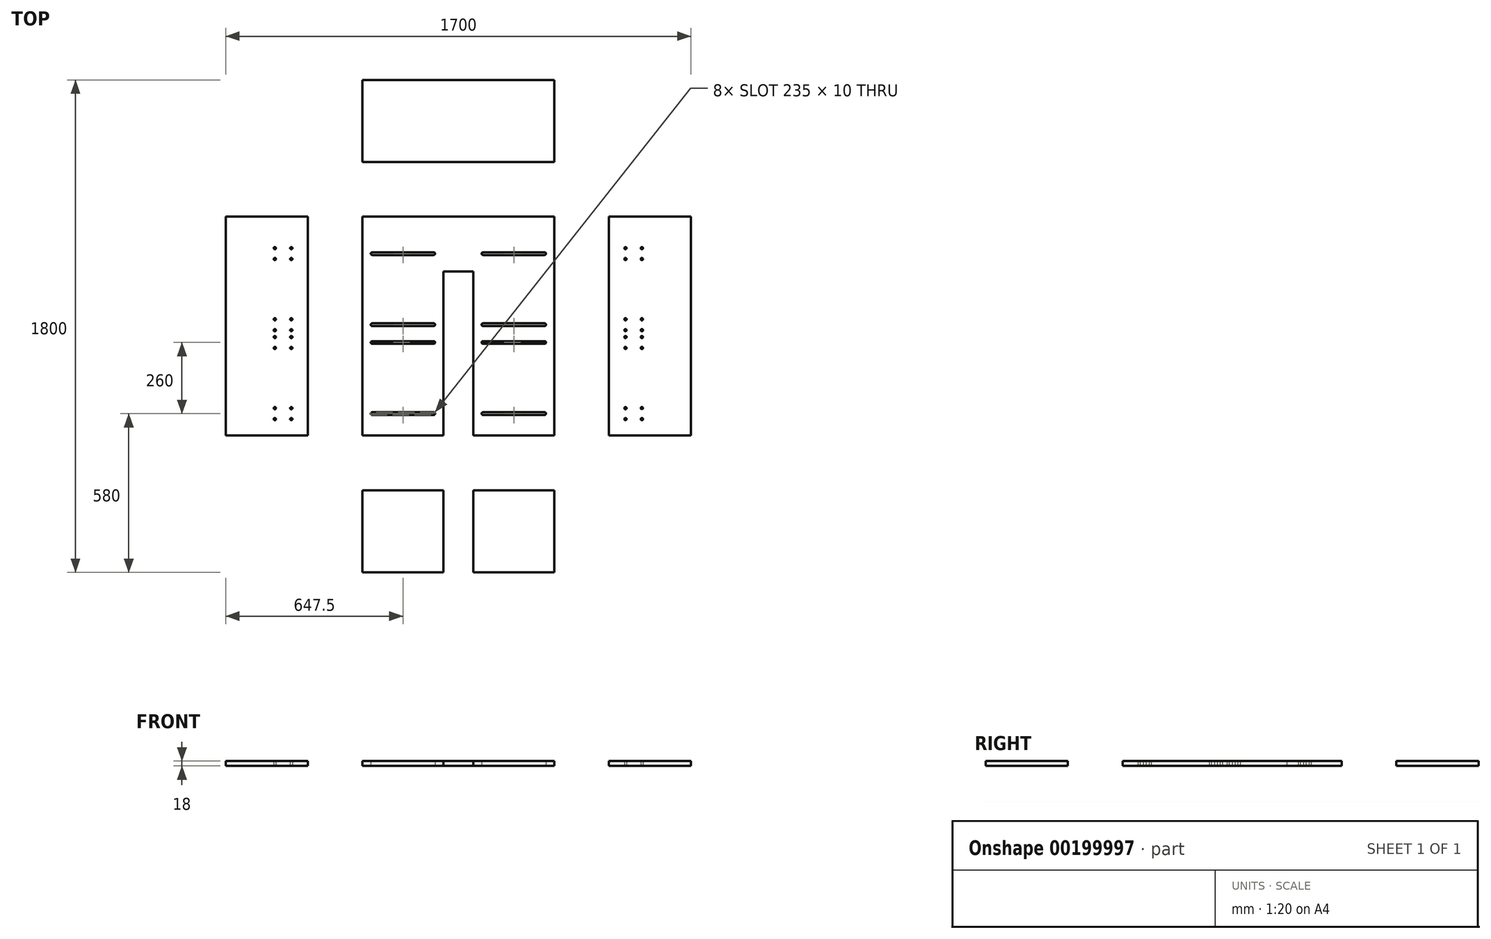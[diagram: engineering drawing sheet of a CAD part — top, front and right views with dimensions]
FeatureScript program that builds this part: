
annotation { "Feature Type Name" : "Feature", "Feature Type Description" : "" }
export const myFeature = defineFeature(function(context is Context, id is Id, definition is map)
    precondition{}
    {
        {
            var Q0;
            Q0=qCreatedBy(makeId("Top.planeOp"),FACE);
            var sketch = newSketch(context, id + "F0", { "sketchPlane" : qUnion([Q0])});
            skLineSegment(sketch, "E0.bottom", {"start": v(0, 0) * mm, "end": v(4000, 0) * mm, "construction": true});
            skLineSegment(sketch, "E0.top", {"start": v(0, 4000) * mm, "end": v(4000, 4000) * mm, "construction": true});
            skLineSegment(sketch, "E0.left", {"start": v(0, 0) * mm, "end": v(0, 4000) * mm, "construction": true});
            skLineSegment(sketch, "E0.right", {"start": v(4000, 0) * mm, "end": v(4000, 4000) * mm, "construction": true});
            skLineSegment(sketch, "E1.bottom", {"start": v(0, 0) * mm, "end": v(1000, 0) * mm, "construction": true});
            skLineSegment(sketch, "E1.top", {"start": v(0, 1000) * mm, "end": v(1000, 1000) * mm, "construction": true});
            skLineSegment(sketch, "E1.left", {"start": v(0, 0) * mm, "end": v(0, 1000) * mm, "construction": true});
            skLineSegment(sketch, "E1.right", {"start": v(1000, 0) * mm, "end": v(1000, 1000) * mm, "construction": true});
            skSolve(sketch);
        }
        {
            var Q0;
            Q0=qCreatedBy(makeId("Top.planeOp"),FACE);
            var sketch = newSketch(context, id + "F1", { "sketchPlane" : qUnion([Q0])});
            skPoint(sketch, "E2", {"position": v(1000, 1000) * mm});
            skLineSegment(sketch, "E3.bottom", {"start": v(1000, 1000) * mm, "end": v(1295, 1000) * mm});
            skLineSegment(sketch, "E3.top", {"start": v(1000, 1800) * mm, "end": v(1700, 1800) * mm});
            skLineSegment(sketch, "E3.left", {"start": v(1000, 1000) * mm, "end": v(1000, 1800) * mm});
            skLineSegment(sketch, "E3.right", {"start": v(1700, 1000) * mm, "end": v(1700, 1800) * mm});
            skLineSegment(sketch, "E4", {"start": v(1405, 1600) * mm, "end": v(1405, 1000) * mm});
            skLineSegment(sketch, "E5", {"start": v(1295, 1000) * mm, "end": v(1295, 1600) * mm});
            skPoint(sketch, "E6", {"position": v(1350, 1000) * mm});
            skLineSegment(sketch, "E7", {"start": v(1295, 1600) * mm, "end": v(1405, 1600) * mm});
            skPoint(sketch, "E8", {"position": v(1350, 1800) * mm});
            skPoint(sketch, "E9", {"position": v(1350, 1600) * mm});
            skLineSegment(sketch, "E10.trimOffspring", {"start": v(1405, 1000) * mm, "end": v(1700, 1000) * mm});
            skLineSegment(sketch, "E11.bottom", {"start": v(800, 1800) * mm, "end": v(500, 1800) * mm});
            skLineSegment(sketch, "E11.top", {"start": v(800, 1000) * mm, "end": v(500, 1000) * mm});
            skLineSegment(sketch, "E11.left", {"start": v(800, 1800) * mm, "end": v(800, 1000) * mm});
            skLineSegment(sketch, "E11.right", {"start": v(500, 1800) * mm, "end": v(500, 1000) * mm});
            skLineSegment(sketch, "E12.bottom", {"start": v(1000, 800) * mm, "end": v(1295, 800) * mm});
            skLineSegment(sketch, "E12.top", {"start": v(1000, 500) * mm, "end": v(1295, 500) * mm});
            skLineSegment(sketch, "E12.left", {"start": v(1000, 800) * mm, "end": v(1000, 500) * mm});
            skLineSegment(sketch, "E12.right", {"start": v(1295, 800) * mm, "end": v(1295, 500) * mm});
            skLineSegment(sketch, "E13.bottom", {"start": v(1000, 2000) * mm, "end": v(1700, 2000) * mm});
            skLineSegment(sketch, "E13.top", {"start": v(1000, 2300) * mm, "end": v(1700, 2300) * mm});
            skLineSegment(sketch, "E13.left", {"start": v(1000, 2000) * mm, "end": v(1000, 2300) * mm});
            skLineSegment(sketch, "E13.right", {"start": v(1700, 2000) * mm, "end": v(1700, 2300) * mm});
            skLineSegment(sketch, "E14.bottom", {"start": v(1405, 800) * mm, "end": v(1700, 800) * mm});
            skLineSegment(sketch, "E14.top", {"start": v(1405, 500) * mm, "end": v(1700, 500) * mm});
            skLineSegment(sketch, "E14.left", {"start": v(1405, 800) * mm, "end": v(1405, 500) * mm});
            skLineSegment(sketch, "E14.right", {"start": v(1700, 800) * mm, "end": v(1700, 500) * mm});
            skLineSegment(sketch, "E15", {"start": v(1350, 195.44) * mm, "end": v(1350, 0) * mm, "construction": true});
            skLineSegment(sketch, "E16", {"start": v(251.7, 1400) * mm, "end": v(84.67, 1400) * mm, "construction": true});
            skPoint(sketch, "E16.startSnap0", {"position": v(500, 1400) * mm});
            skLineSegment(sketch, "E17.MirrorCS", {"start": v(1900, 1000) * mm, "end": v(2200, 1000) * mm});
            skLineSegment(sketch, "E18.MirrorCS", {"start": v(1900, 1800) * mm, "end": v(1900, 1000) * mm});
            skLineSegment(sketch, "E19.MirrorCS", {"start": v(1900, 1800) * mm, "end": v(2200, 1800) * mm});
            skLineSegment(sketch, "E20.MirrorCS", {"start": v(2200, 1800) * mm, "end": v(2200, 1000) * mm});
            skPoint(sketch, "E21", {"position": v(1147.5, 1000) * mm});
            skPoint(sketch, "E22", {"position": v(1552.5, 1000) * mm});
            skPoint(sketch, "E23", {"position": v(1147.5, 800) * mm});
            skPoint(sketch, "E24", {"position": v(1000, 650) * mm});
            skPoint(sketch, "E25", {"position": v(650, 1000) * mm});
            skPoint(sketch, "E26", {"position": v(1295, 650) * mm});
            skPoint(sketch, "E27", {"position": v(1405, 650) * mm});
            skPoint(sketch, "E28", {"position": v(1700, 650) * mm});
            skPoint(sketch, "E29", {"position": v(1552.5, 800) * mm});
            skPoint(sketch, "E30", {"position": v(1350, 2300) * mm});
            skPoint(sketch, "E31", {"position": v(1147.5, 2300) * mm});
            skPoint(sketch, "E32", {"position": v(1552.5, 2300) * mm});
            skPoint(sketch, "E33", {"position": v(2200, 1400) * mm});
            skPoint(sketch, "E34", {"position": v(2050, 1000) * mm});
            skPoint(sketch, "E35", {"position": v(1405, 1300) * mm});
            skPoint(sketch, "E36", {"position": v(1295, 1300) * mm});
            skLineSegment(sketch, "E37", {"start": v(1035, 1080) * mm, "end": v(1260, 1080) * mm});
            skPoint(sketch, "E38", {"position": v(1147.5, 1080) * mm});
            skLineSegment(sketch, "E39", {"start": v(1035, 1665) * mm, "end": v(1260, 1665) * mm});
            skPoint(sketch, "E40", {"position": v(1147.5, 1665) * mm});
            skLineSegment(sketch, "E41", {"start": v(1035, 1405) * mm, "end": v(1260, 1405) * mm});
            skPoint(sketch, "E42", {"position": v(1147.5, 1405) * mm});
            skLineSegment(sketch, "E43", {"start": v(1035, 1340) * mm, "end": v(1260, 1340) * mm});
            skPoint(sketch, "E44", {"position": v(1147.5, 1340) * mm});
            skLineSegment(sketch, "E45.bottom", {"start": v(679.65, 1060) * mm, "end": v(739.65, 1060) * mm, "construction": true});
            skLineSegment(sketch, "E45.top", {"start": v(679.65, 1100) * mm, "end": v(739.65, 1100) * mm, "construction": true});
            skLineSegment(sketch, "E45.left", {"start": v(679.65, 1100) * mm, "end": v(679.65, 1060) * mm});
            skLineSegment(sketch, "E45.right", {"start": v(739.65, 1100) * mm, "end": v(739.65, 1060) * mm});
            skPoint(sketch, "E46", {"position": v(739.65, 1080) * mm});
            skLineSegment(sketch, "E47.bottom", {"start": v(679.65, 1360) * mm, "end": v(739.65, 1360) * mm});
            skLineSegment(sketch, "E47.top", {"start": v(679.65, 1320) * mm, "end": v(739.65, 1320) * mm, "construction": true});
            skLineSegment(sketch, "E47.left", {"start": v(679.65, 1360) * mm, "end": v(679.65, 1320) * mm});
            skLineSegment(sketch, "E47.right", {"start": v(739.65, 1360) * mm, "end": v(739.65, 1320) * mm});
            skLineSegment(sketch, "E48.bottom", {"start": v(679.65, 1425) * mm, "end": v(739.65, 1425) * mm, "construction": true});
            skLineSegment(sketch, "E48.top", {"start": v(679.65, 1385) * mm, "end": v(739.65, 1385) * mm, "construction": true});
            skLineSegment(sketch, "E48.left", {"start": v(679.65, 1425) * mm, "end": v(679.65, 1385) * mm});
            skLineSegment(sketch, "E48.right", {"start": v(739.65, 1425) * mm, "end": v(739.65, 1385) * mm});
            skLineSegment(sketch, "E49.bottom", {"start": v(679.65, 1685) * mm, "end": v(739.65, 1685) * mm, "construction": true});
            skLineSegment(sketch, "E49.top", {"start": v(679.65, 1645) * mm, "end": v(739.65, 1645) * mm, "construction": true});
            skLineSegment(sketch, "E49.left", {"start": v(679.65, 1685) * mm, "end": v(679.65, 1645) * mm});
            skLineSegment(sketch, "E49.right", {"start": v(739.65, 1685) * mm, "end": v(739.65, 1645) * mm});
            skPoint(sketch, "E50", {"position": v(739.65, 1665) * mm});
            skPoint(sketch, "E51", {"position": v(739.65, 1405) * mm});
            skPoint(sketch, "E52", {"position": v(739.65, 1340) * mm});
            skCircle(sketch, "E53", {"center": v(739.65, 1685) * mm, "radius": 4 * mm});
            skCircle(sketch, "E54", {"center": v(739.65, 1645) * mm, "radius": 4 * mm});
            skCircle(sketch, "E55", {"center": v(739.65, 1425) * mm, "radius": 4 * mm});
            skCircle(sketch, "E56", {"center": v(739.65, 1385) * mm, "radius": 4 * mm});
            skCircle(sketch, "E57", {"center": v(739.65, 1360) * mm, "radius": 4 * mm});
            skCircle(sketch, "E58", {"center": v(739.65, 1320) * mm, "radius": 4 * mm});
            skCircle(sketch, "E59", {"center": v(739.65, 1100) * mm, "radius": 4 * mm});
            skCircle(sketch, "E60", {"center": v(739.65, 1060) * mm, "radius": 4 * mm});
            skLineSegment(sketch, "E61", {"start": v(709.65, 908.26) * mm, "end": v(709.65, 656.92) * mm, "construction": true});
            skPoint(sketch, "E61.startSnap0", {"position": v(709.65, 1060) * mm});
            skCircle(sketch, "E62.MirrorC", {"center": v(679.65, 1060) * mm, "radius": 4 * mm});
            skCircle(sketch, "E63.MirrorC", {"center": v(679.65, 1100) * mm, "radius": 4 * mm});
            skCircle(sketch, "E64.MirrorC", {"center": v(679.65, 1320) * mm, "radius": 4 * mm});
            skCircle(sketch, "E65.MirrorC", {"center": v(679.65, 1360) * mm, "radius": 4 * mm});
            skCircle(sketch, "E66.MirrorC", {"center": v(679.65, 1425) * mm, "radius": 4 * mm});
            skCircle(sketch, "E67.MirrorC", {"center": v(679.65, 1385) * mm, "radius": 4 * mm});
            skCircle(sketch, "E68.MirrorC", {"center": v(679.65, 1645) * mm, "radius": 4 * mm});
            skCircle(sketch, "E69.MirrorC", {"center": v(679.65, 1685) * mm, "radius": 4 * mm});
            skLineSegment(sketch, "E70.MirrorCS", {"start": v(1665, 1080) * mm, "end": v(1440, 1080) * mm});
            skLineSegment(sketch, "E71.MirrorCS", {"start": v(1665, 1340) * mm, "end": v(1440, 1340) * mm});
            skLineSegment(sketch, "E72.MirrorCS", {"start": v(1665, 1405) * mm, "end": v(1440, 1405) * mm});
            skLineSegment(sketch, "E73.MirrorCS", {"start": v(1665, 1665) * mm, "end": v(1440, 1665) * mm});
            skCircle(sketch, "E74.MirrorC", {"center": v(2020.35, 1685) * mm, "radius": 4 * mm});
            skCircle(sketch, "E75.MirrorC", {"center": v(1960.35, 1685) * mm, "radius": 4 * mm});
            skCircle(sketch, "E76.MirrorC", {"center": v(2020.35, 1645) * mm, "radius": 4 * mm});
            skCircle(sketch, "E77.MirrorC", {"center": v(1960.35, 1645) * mm, "radius": 4 * mm});
            skCircle(sketch, "E78.MirrorC", {"center": v(1960.35, 1425) * mm, "radius": 4 * mm});
            skCircle(sketch, "E79.MirrorC", {"center": v(1960.35, 1385) * mm, "radius": 4 * mm});
            skCircle(sketch, "E80.MirrorC", {"center": v(1960.35, 1360) * mm, "radius": 4 * mm});
            skCircle(sketch, "E81.MirrorC", {"center": v(1960.35, 1320) * mm, "radius": 4 * mm});
            skCircle(sketch, "E82.MirrorC", {"center": v(2020.35, 1320) * mm, "radius": 4 * mm});
            skCircle(sketch, "E83.MirrorC", {"center": v(1960.35, 1100) * mm, "radius": 4 * mm});
            skCircle(sketch, "E84.MirrorC", {"center": v(2020.35, 1100) * mm, "radius": 4 * mm});
            skCircle(sketch, "E85.MirrorC", {"center": v(2020.35, 1060) * mm, "radius": 4 * mm});
            skCircle(sketch, "E86.MirrorC", {"center": v(1960.35, 1060) * mm, "radius": 4 * mm});
            skCircle(sketch, "E87.MirrorC", {"center": v(2020.35, 1360) * mm, "radius": 4 * mm});
            skCircle(sketch, "E88.MirrorC", {"center": v(2020.35, 1385) * mm, "radius": 4 * mm});
            skCircle(sketch, "E89.MirrorC", {"center": v(2020.35, 1425) * mm, "radius": 4 * mm});
            skArc(sketch, "E90.0.startCap", {"start": v(1260, 1670) * mm, "mid": v(1265, 1665) * mm, "end": v(1260, 1660) * mm});
            skArc(sketch, "E90.0.endCap", {"start": v(1035, 1660) * mm, "mid": v(1030, 1665) * mm, "end": v(1035, 1670) * mm});
            skLineSegment(sketch, "E90.0.left", {"start": v(1035, 1660) * mm, "end": v(1260, 1660) * mm});
            skLineSegment(sketch, "E90.0.right", {"start": v(1035, 1670) * mm, "end": v(1260, 1670) * mm});
            skArc(sketch, "E90.1.startCap", {"start": v(1440, 1660) * mm, "mid": v(1435, 1665) * mm, "end": v(1440, 1670) * mm});
            skArc(sketch, "E90.1.endCap", {"start": v(1665, 1670) * mm, "mid": v(1670, 1665) * mm, "end": v(1665, 1660) * mm});
            skLineSegment(sketch, "E90.1.left", {"start": v(1665, 1670) * mm, "end": v(1440, 1670) * mm});
            skLineSegment(sketch, "E90.1.right", {"start": v(1665, 1660) * mm, "end": v(1440, 1660) * mm});
            skArc(sketch, "E90.2.startCap", {"start": v(1440, 1400) * mm, "mid": v(1435, 1405) * mm, "end": v(1440, 1410) * mm});
            skArc(sketch, "E90.2.endCap", {"start": v(1665, 1410) * mm, "mid": v(1670, 1405) * mm, "end": v(1665, 1400) * mm});
            skLineSegment(sketch, "E90.2.left", {"start": v(1665, 1410) * mm, "end": v(1440, 1410) * mm});
            skLineSegment(sketch, "E90.2.right", {"start": v(1665, 1400) * mm, "end": v(1440, 1400) * mm});
            skArc(sketch, "E90.3.startCap", {"start": v(1440, 1335) * mm, "mid": v(1435, 1340) * mm, "end": v(1440, 1345) * mm});
            skArc(sketch, "E90.3.endCap", {"start": v(1665, 1345) * mm, "mid": v(1670, 1340) * mm, "end": v(1665, 1335) * mm});
            skLineSegment(sketch, "E90.3.left", {"start": v(1665, 1345) * mm, "end": v(1440, 1345) * mm});
            skLineSegment(sketch, "E90.3.right", {"start": v(1665, 1335) * mm, "end": v(1440, 1335) * mm});
            skArc(sketch, "E90.4.startCap", {"start": v(1260, 1345) * mm, "mid": v(1265, 1340) * mm, "end": v(1260, 1335) * mm});
            skArc(sketch, "E90.4.endCap", {"start": v(1035, 1335) * mm, "mid": v(1030, 1340) * mm, "end": v(1035, 1345) * mm});
            skLineSegment(sketch, "E90.4.left", {"start": v(1035, 1335) * mm, "end": v(1260, 1335) * mm});
            skLineSegment(sketch, "E90.4.right", {"start": v(1035, 1345) * mm, "end": v(1260, 1345) * mm});
            skArc(sketch, "E90.5.startCap", {"start": v(1035, 1075) * mm, "mid": v(1030, 1080) * mm, "end": v(1035, 1085) * mm});
            skArc(sketch, "E90.5.endCap", {"start": v(1260, 1085) * mm, "mid": v(1265, 1080) * mm, "end": v(1260, 1075) * mm});
            skLineSegment(sketch, "E90.5.left", {"start": v(1035, 1085) * mm, "end": v(1260, 1085) * mm});
            skLineSegment(sketch, "E90.5.right", {"start": v(1035, 1075) * mm, "end": v(1260, 1075) * mm});
            skArc(sketch, "E90.6.startCap", {"start": v(1665, 1085) * mm, "mid": v(1670, 1080) * mm, "end": v(1665, 1075) * mm});
            skArc(sketch, "E90.6.endCap", {"start": v(1440, 1075) * mm, "mid": v(1435, 1080) * mm, "end": v(1440, 1085) * mm});
            skLineSegment(sketch, "E90.6.left", {"start": v(1665, 1075) * mm, "end": v(1440, 1075) * mm});
            skLineSegment(sketch, "E90.6.right", {"start": v(1665, 1085) * mm, "end": v(1440, 1085) * mm});
            skArc(sketch, "E90.7.startCap", {"start": v(1260, 1410) * mm, "mid": v(1265, 1405) * mm, "end": v(1260, 1400) * mm});
            skArc(sketch, "E90.7.endCap", {"start": v(1035, 1400) * mm, "mid": v(1030, 1405) * mm, "end": v(1035, 1410) * mm});
            skLineSegment(sketch, "E90.7.left", {"start": v(1035, 1400) * mm, "end": v(1260, 1400) * mm});
            skLineSegment(sketch, "E90.7.right", {"start": v(1035, 1410) * mm, "end": v(1260, 1410) * mm});
            skPoint(sketch, "E91", {"position": v(1350, 1300) * mm});
            skSolve(sketch);
        }
        {
            var Q0;
            Q0=makeQuery(id+"F1.imprint","IMPRINT",FACE,{"disambiguationData":[TD([[makeQuery(id+"F1.imprint","IMPRINT",EDGE,{"derivedFrom":sQuery(id+"F1.wireOp",EDGE,"E11.bottom")}),1.0]])]});
            var Q1;
            Q1=makeQuery(id+"F1.imprint","IMPRINT",FACE,{"disambiguationData":[TD([[makeQuery(id+"F1.imprint","IMPRINT",EDGE,{"derivedFrom":sQuery(id+"F1.wireOp",EDGE,"E3.bottom")}),1.0]])]});
            var Q2;
            Q2=makeQuery(id+"F1.imprint","IMPRINT",FACE,{"disambiguationData":[TD([[makeQuery(id+"F1.imprint","IMPRINT",EDGE,{"derivedFrom":sQuery(id+"F1.wireOp",EDGE,"E17.MirrorCS")}),1.0]])]});
            var Q3;
            Q3=makeQuery(id+"F1.imprint","IMPRINT",FACE,{"disambiguationData":[TD([[makeQuery(id+"F1.imprint","IMPRINT",EDGE,{"derivedFrom":sQuery(id+"F1.wireOp",EDGE,"E14.bottom")}),-1.0]])]});
            var Q4;
            Q4=makeQuery(id+"F1.imprint","IMPRINT",FACE,{"disambiguationData":[TD([[makeQuery(id+"F1.imprint","IMPRINT",EDGE,{"derivedFrom":sQuery(id+"F1.wireOp",EDGE,"E12.bottom")}),-1.0]])]});
            var Q5;
            Q5=makeQuery(id+"F1.imprint","IMPRINT",FACE,{"disambiguationData":[TD([[makeQuery(id+"F1.imprint","IMPRINT",EDGE,{"derivedFrom":sQuery(id+"F1.wireOp",EDGE,"E13.bottom")}),1.0]])]});
            extrude(context, id + "F2", {"entities" : qUnion([Q0, Q1, Q2, Q3, Q4, Q5]), "depth" : 18 * mm});
        }
    });
